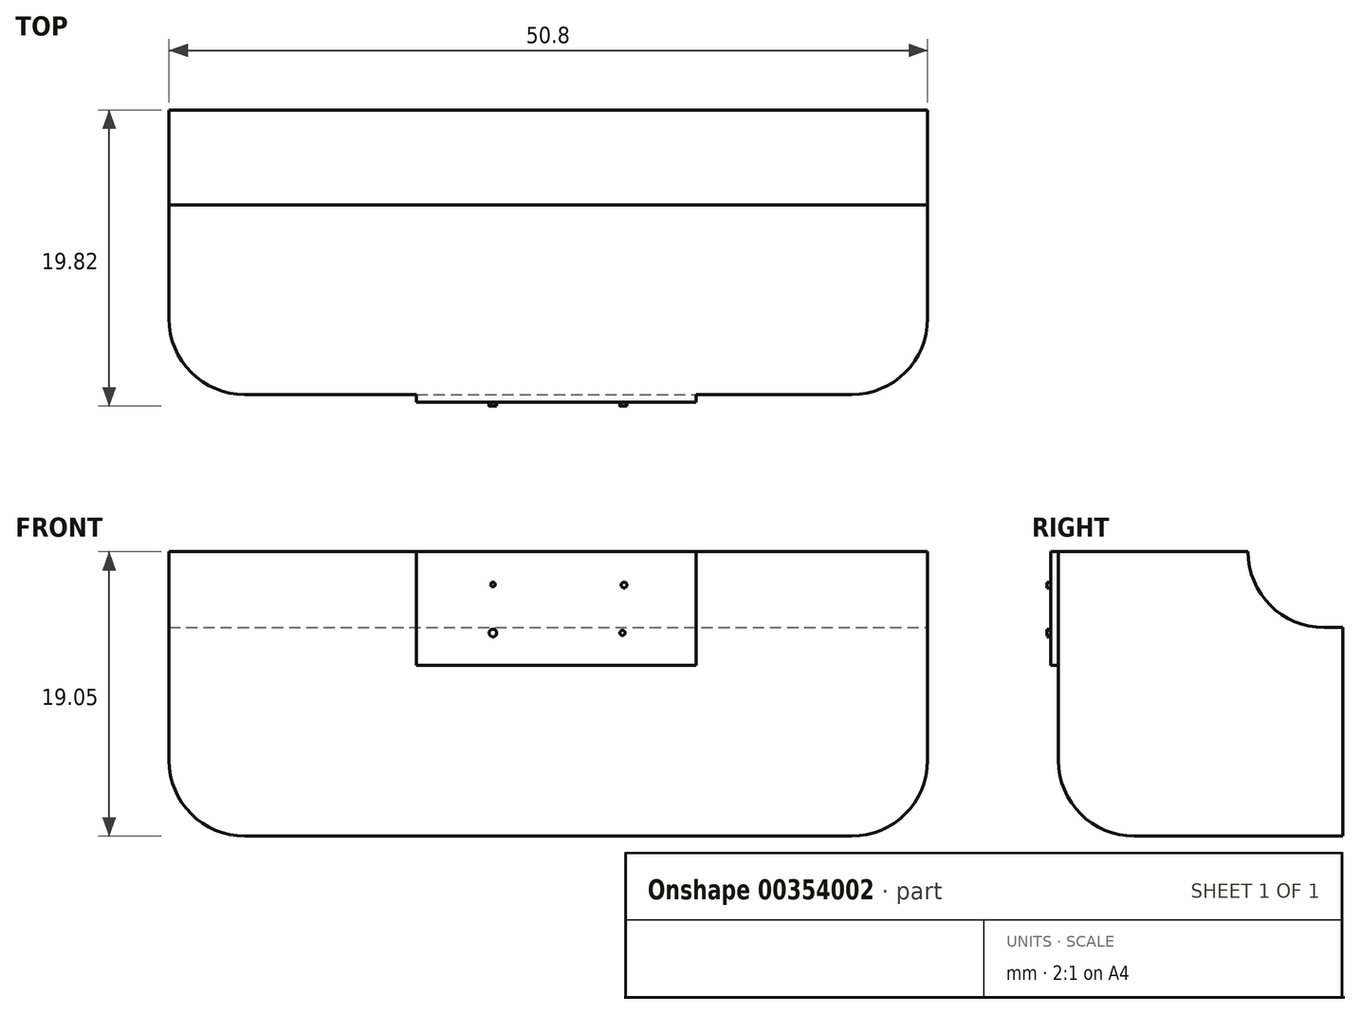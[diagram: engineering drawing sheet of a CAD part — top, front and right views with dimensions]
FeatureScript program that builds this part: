
annotation { "Feature Type Name" : "Feature", "Feature Type Description" : "" }
export const myFeature = defineFeature(function(context is Context, id is Id, definition is map)
    precondition{}
    {
        {
            var Q0;
            Q0=qCreatedBy(makeId("Top.planeOp"),FACE);
            var sketch = newSketch(context, id + "F0", { "sketchPlane" : qUnion([Q0])});
            skLineSegment(sketch, "E0.bottom", {"start": v(25.4, -9.52) * mm, "end": v(-25.4, -9.53) * mm});
            skLineSegment(sketch, "E0.top", {"start": v(25.4, 9.53) * mm, "end": v(-25.4, 9.52) * mm});
            skLineSegment(sketch, "E0.left", {"start": v(25.4, -9.52) * mm, "end": v(25.4, 9.53) * mm});
            skLineSegment(sketch, "E0.right", {"start": v(-25.4, -9.53) * mm, "end": v(-25.4, 9.52) * mm});
            skPoint(sketch, "E0.middle", {"position": v(0, 0) * mm});
            skSolve(sketch);
        }
        {
            var Q0;
            Q0 = qSketchRegion(id + "F0", true);
            extrude(context, id + "F1", {"entities" : qUnion([Q0]), "depth" : 19.05 * mm});
        }
        {
            var Q0;
            Q0=makeQuery(id+"F1.opExtrude","SWEPT_EDGE",EDGE,{"disambiguationData":[OSD([sQuery(id+"F0.wireOp",EDGE,"E0.bottom"),sQuery(id+"F0.wireOp",EDGE,"E0.right")])]});
            var Q1;
            Q1=makeQuery(id+"F1.opExtrude","SWEPT_EDGE",EDGE,{"disambiguationData":[OSD([sQuery(id+"F0.wireOp",EDGE,"E0.bottom"),sQuery(id+"F0.wireOp",EDGE,"E0.left")])]});
            fillet(context, id + "F2", {"entities" : qUnion([Q0, Q1]), "radius" : 5.08 * mm, "tangentPropagation" : true, "allowEdgeOverflow" : false});
        }
        {
            var Q0;
            Q0=makeQuery(id+"F1.opExtrude","CAP_EDGE",EDGE,{"disambiguationData":[OSD([sQuery(id+"F0.wireOp",EDGE,"E0.left")])],"isStart":true});
            fillet(context, id + "F3", {"entities" : qUnion([Q0]), "radius" : 5.08 * mm, "tangentPropagation" : true, "allowEdgeOverflow" : false});
        }
        {
            var Q0;
            Q0=makeQuery(id+"F1.opExtrude","SWEPT_FACE",FACE,{"disambiguationData":[OSD([sQuery(id+"F0.wireOp",EDGE,"E0.bottom")])]});
            var sketch = newSketch(context, id + "F4", { "sketchPlane" : qUnion([Q0])});
            skLineSegment(sketch, "E1.bottom", {"start": v(-8.82, 11.43) * mm, "end": v(9.92, 11.43) * mm});
            skLineSegment(sketch, "E1.top", {"start": v(-8.82, 19.05) * mm, "end": v(9.92, 19.05) * mm});
            skLineSegment(sketch, "E1.left", {"start": v(-8.82, 11.43) * mm, "end": v(-8.82, 19.05) * mm});
            skLineSegment(sketch, "E1.right", {"start": v(9.92, 11.43) * mm, "end": v(9.92, 19.05) * mm});
            skSolve(sketch);
        }
        {
            var Q0;
            Q0 = qSketchRegion(id + "F4", true);
            extrude(context, id + "F5", {"entities" : qUnion([Q0]), "operationType" : NewBodyOperationType.ADD, "depth" : 0.5 * mm});
        }
        {
            var Q0;
            Q0=makeQuery(id+"F5.opExtrude","CAP_FACE",FACE,{"disambiguationData":[OSD([sQuery(id+"F4.wireOp",EDGE,"E1.bottom"),sQuery(id+"F4.wireOp",EDGE,"E1.top"),sQuery(id+"F4.wireOp",EDGE,"E1.left"),sQuery(id+"F4.wireOp",EDGE,"E1.right")])],"isStart":false});
            var sketch = newSketch(context, id + "F6", { "sketchPlane" : qUnion([Q0])});
            skCircle(sketch, "E2", {"center": v(4.97, 13.6) * mm, "radius": 0.17 * mm});
            skCircle(sketch, "E3", {"center": v(-3.7, 13.6) * mm, "radius": 0.25 * mm});
            skCircle(sketch, "E4", {"center": v(5.07, 16.82) * mm, "radius": 0.2 * mm});
            skCircle(sketch, "E5", {"center": v(-3.7, 16.85) * mm, "radius": 0.15 * mm});
            skSolve(sketch);
        }
        {
            var Q0;
            Q0 = qSketchRegion(id + "F6", true);
            extrude(context, id + "F7", {"entities" : qUnion([Q0]), "operationType" : NewBodyOperationType.ADD, "depth" : 0.25 * mm});
        }
        {
            var Q0;
            Q0=makeQuery(id+"F1.opExtrude","SWEPT_FACE",FACE,{"disambiguationData":[OSD([sQuery(id+"F0.wireOp",EDGE,"E0.left")])]});
            var sketch = newSketch(context, id + "F8", { "sketchPlane" : qUnion([Q0])});
            skLineSegment(sketch, "E6", {"start": v(3.18, 13.97) * mm, "end": v(9.53, 13.97) * mm});
            skPoint(sketch, "E7.start.orphan", {"position": v(2.54, 19.05) * mm});
            skLineSegment(sketch, "E8", {"start": v(9.53, 13.97) * mm, "end": v(9.53, 19.05) * mm});
            skLineSegment(sketch, "E9", {"start": v(3.18, 13.97) * mm, "end": v(3.18, 19.05) * mm});
            skLineSegment(sketch, "E10", {"start": v(3.18, 19.05) * mm, "end": v(9.53, 19.05) * mm});
            skSolve(sketch);
        }
        {
            var Q0;
            Q0 = qSketchRegion(id + "F8", true);
            extrude(context, id + "F9", {"entities" : qUnion([Q0]), "operationType" : NewBodyOperationType.REMOVE, "oppositeDirection" : true, "depth" : 50.8 * mm});
        }
        {
            var Q0;
            Q0=makeQuery(id+"F9.boolean.opBoolean","COPY",EDGE,{"derivedFrom":makeQuery(id+"F9.opExtrude","SWEPT_EDGE",EDGE,{"disambiguationData":[OSD([sQuery(id+"F8.wireOp",EDGE,"E6"),sQuery(id+"F8.wireOp",EDGE,"E9")])]})});
            fillet(context, id + "F10", {"entities" : qUnion([Q0]), "radius" : 5.08 * mm, "tangentPropagation" : true, "allowEdgeOverflow" : false});
        }
    });
